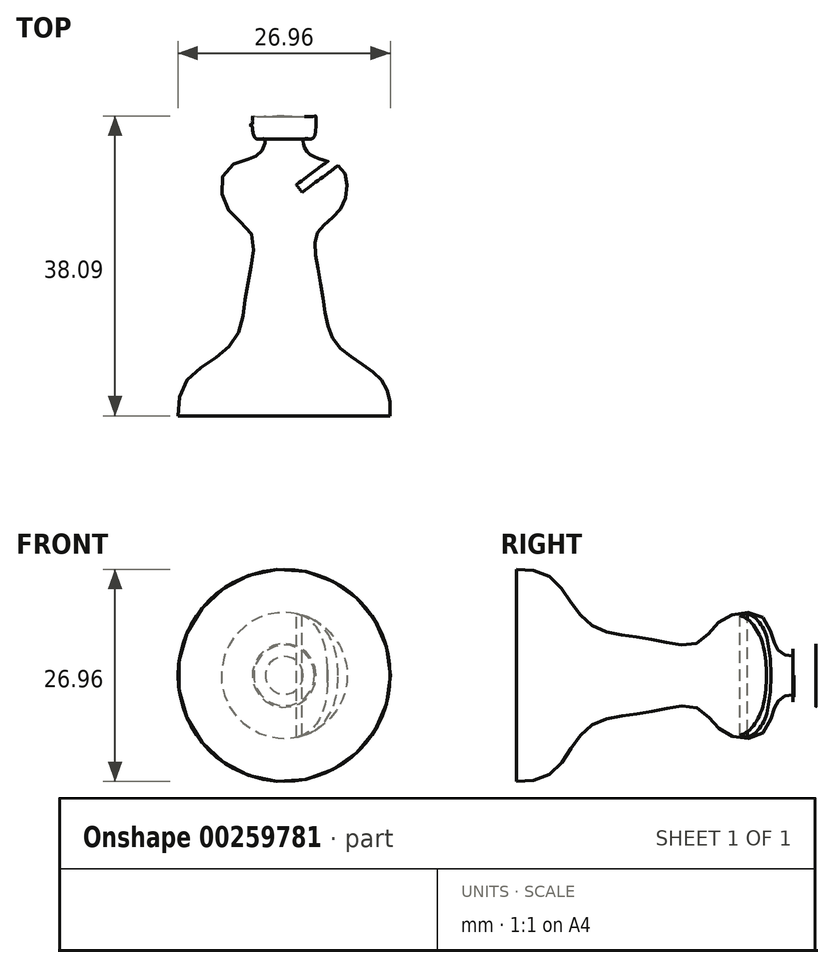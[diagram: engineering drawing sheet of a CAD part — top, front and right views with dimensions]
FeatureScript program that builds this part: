
annotation { "Feature Type Name" : "Feature", "Feature Type Description" : "" }
export const myFeature = defineFeature(function(context is Context, id is Id, definition is map)
    precondition{}
    {
        {
            var Q0;
            Q0=qCreatedBy(makeId("Top.planeOp"),FACE);
            var sketch = newSketch(context, id + "F0", { "sketchPlane" : qUnion([Q0])});
            skLineSegment(sketch, "E0", {"start": v(0, 0) * mm, "end": v(0, 38.08) * mm});
            skFitSpline(sketch, "E1", {"points": [v(0, 38.08) * mm, v(3.96, 38.08) * mm, v(4, 38.08) * mm, v(3.69, 35.27) * mm, v(2.54, 35.22) * mm, v(3.15, 33.32) * mm, v(7.23, 31.47) * mm, v(7.27, 26.42) * mm, v(4.14, 23.05) * mm, v(4.68, 16.57) * mm, v(6.48, 9.37) * mm, v(11.7, 5.22) * mm, v(13.46, 0) * mm], "startDerivative": vector(61.95, -2.62) * mm, "endDerivative": vector(-3.52, -70.56) * mm});
            skLineSegment(sketch, "E2", {"start": v(0, 0) * mm, "end": v(13.46, 0) * mm});
            skSolve(sketch);
        }
        {
            var Q0;
            Q0=makeQuery(id+"F0.imprint","IMPRINT",FACE,{"disambiguationData":[TD([[makeQuery(id+"F0.imprint","IMPRINT",EDGE,{"derivedFrom":sQuery(id+"F0.wireOp",EDGE,"E0")}),-1.0]])]});
            var Q1;
            Q1=sQuery(id+"F0.wireOp",EDGE,"E0");
            revolve(context, id + "F1", {"entities" : qUnion([Q0]), "axis" : qUnion([Q1]), "revolveType" : RevolveType.FULL});
        }
        {
            var Q0;
            Q0=makeQuery(id+"F0.imprint","IMPRINT",FACE,{"disambiguationData":[TD([[makeQuery(id+"F0.imprint","IMPRINT",EDGE,{"derivedFrom":sQuery(id+"F0.wireOp",EDGE,"E0")}),-1.0]])]});
            var sketch = newSketch(context, id + "F2", { "sketchPlane" : qUnion([Q0])});
            skLineSegment(sketch, "E3", {"start": v(5.51, 32.33) * mm, "end": v(1.54, 29.37) * mm});
            skLineSegment(sketch, "E4", {"start": v(1.54, 29.37) * mm, "end": v(2.28, 28.38) * mm});
            skLineSegment(sketch, "E5", {"start": v(2.28, 28.38) * mm, "end": v(7.58, 32.33) * mm});
            skLineSegment(sketch, "E6", {"start": v(5.51, 32.33) * mm, "end": v(7.58, 32.33) * mm});
            skSolve(sketch);
        }
        {
            var Q0;
            Q0 = qSketchRegion(id + "F2", true);
            extrude(context, id + "F3", {"entities" : qUnion([Q0]), "operationType" : NewBodyOperationType.REMOVE, "oppositeDirection" : true, "depth" : 25.4 * mm});
        }
        {
            var Q0;
            Q0 = qSketchRegion(id + "F2", true);
            extrude(context, id + "F4", {"entities" : qUnion([Q0]), "operationType" : NewBodyOperationType.REMOVE, "depth" : 25.4 * mm});
        }
    });
